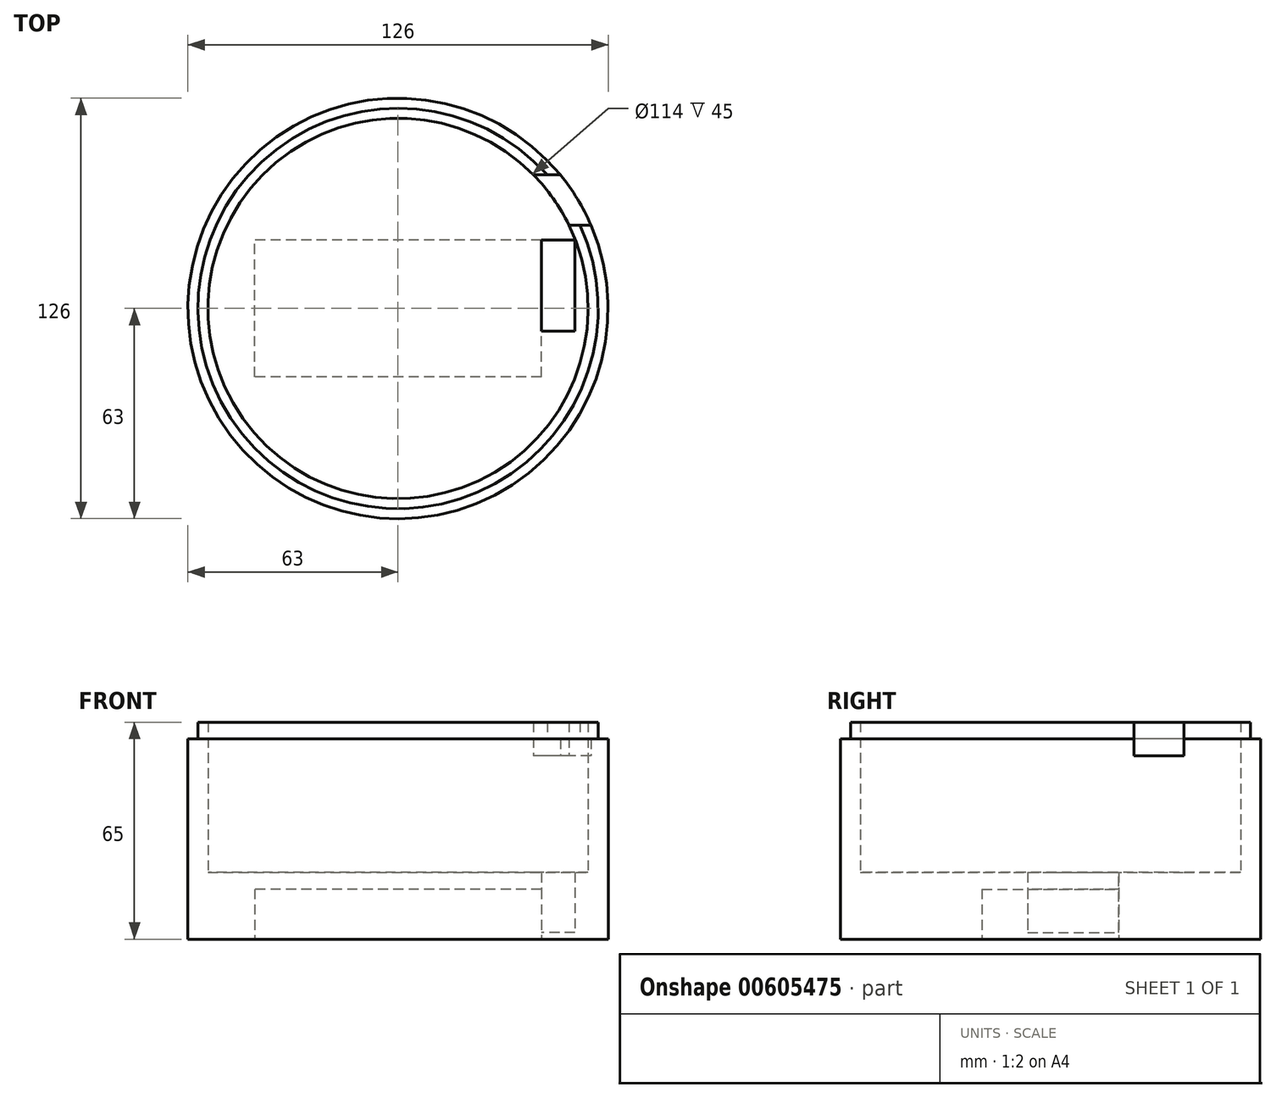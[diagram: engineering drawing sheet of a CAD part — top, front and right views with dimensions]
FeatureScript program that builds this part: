
annotation { "Feature Type Name" : "Feature", "Feature Type Description" : "" }
export const myFeature = defineFeature(function(context is Context, id is Id, definition is map)
    precondition{}
    {
        {
            var Q0;
            Q0=qCreatedBy(makeId("Top.planeOp"),FACE);
            var sketch = newSketch(context, id + "F0", { "sketchPlane" : qUnion([Q0])});
            skCircle(sketch, "E0", {"center": v(0, 0) * mm, "radius": 63 * mm});
            skCircle(sketch, "E1", {"center": v(0, 0) * mm, "radius": 60 * mm});
            skSolve(sketch);
        }
        {
            var Q0;
            Q0=qCreatedBy(makeId("Top.planeOp"),FACE);
            var sketch = newSketch(context, id + "F1", { "sketchPlane" : qUnion([Q0])});
            skCircle(sketch, "E2", {"center": v(0, 0) * mm, "radius": 57 * mm});
            skCircle(sketch, "E3", {"center": v(0, 0) * mm, "radius": 60 * mm});
            skSolve(sketch);
        }
        {
            var Q0;
            Q0=makeQuery(id+"F0.imprint","IMPRINT",FACE,{"disambiguationData":[TD([[makeQuery(id+"F0.imprint","IMPRINT",EDGE,{"derivedFrom":sQuery(id+"F0.wireOp",EDGE,"E0")}),1.0]])]});
            extrude(context, id + "F2", {"entities" : qUnion([Q0]), "depth" : 60 * mm, "offsetDistance" : 25 * mm});
        }
        {
            var Q0;
            Q0=qSketchRegion(id+"F1",true);
            extrude(context, id + "F3", {"entities" : qUnion([Q0]), "operationType" : NewBodyOperationType.ADD, "depth" : 65 * mm, "offsetDistance" : 25 * mm});
        }
        {
            var Q0;
            Q0=qCreatedBy(makeId("Top.planeOp"),FACE);
            var sketch = newSketch(context, id + "F4", { "sketchPlane" : qUnion([Q0])});
            skCircle(sketch, "E4", {"center": v(0, 0) * mm, "radius": 57 * mm});
            skSolve(sketch);
        }
        {
            var Q0;
            Q0=qSketchRegion(id+"F4",true);
            var Q1;
            Q1=qSketchRegion(id+"F7",true);
            extrude(context, id + "F5", {"entities" : qUnion([Q0, Q1]), "operationType" : NewBodyOperationType.ADD, "depth" : 60 * mm, "offsetDistance" : 25 * mm});
        }
        {
            var Q0;
            Q0=qCreatedBy(makeId("Top.planeOp"),FACE);
            cPlane(context, id + "F6", {"entities" : qUnion([Q0]), "cplaneType" : CPlaneType.OFFSET, "offset" : 45 * mm, "width" : 150 * mm, "height" : 150 * mm});
        }
        {
            var Q0;
            Q0=qCreatedBy(id+"F6.planeOp",FACE);
            var sketch = newSketch(context, id + "F7", { "sketchPlane" : qUnion([Q0])});
            skCircle(sketch, "E5", {"center": v(0, 0) * mm, "radius": 57 * mm});
            skSolve(sketch);
        }
        {
            var Q0;
            Q0=qSketchRegion(id+"F7",true);
            extrude(context, id + "F8", {"entities" : qUnion([Q0]), "operationType" : NewBodyOperationType.REMOVE, "oppositeDirection" : true, "depth" : 40 * mm, "offsetDistance" : 25 * mm});
        }
        {
            var Q0;
            Q0=qCreatedBy(makeId("Right.planeOp"),FACE);
            var sketch = newSketch(context, id + "F9", { "sketchPlane" : qUnion([Q0])});
            skLineSegment(sketch, "E6", {"start": v(0, 0) * mm, "end": v(25, 0) * mm, "construction": true});
            skLineSegment(sketch, "E7", {"start": v(25, 0) * mm, "end": v(25, 65) * mm, "construction": true});
            skLineSegment(sketch, "E8.bottom", {"start": v(25, 65) * mm, "end": v(40, 65) * mm});
            skLineSegment(sketch, "E8.top", {"start": v(25, 55) * mm, "end": v(40, 55) * mm});
            skLineSegment(sketch, "E8.left", {"start": v(25, 65) * mm, "end": v(25, 55) * mm});
            skLineSegment(sketch, "E8.right", {"start": v(40, 65) * mm, "end": v(40, 55) * mm});
            skSolve(sketch);
        }
        {
            var Q0;
            Q0=makeQuery(id+"F9.imprint","IMPRINT",FACE,{"disambiguationData":[TD([[makeQuery(id+"F9.imprint","IMPRINT",EDGE,{"derivedFrom":sQuery(id+"F9.wireOp",EDGE,"E8.bottom")}),-1.0]])]});
            extrude(context, id + "F10", {"entities" : qUnion([Q0]), "operationType" : NewBodyOperationType.REMOVE, "depth" : 279.5 * mm, "offsetDistance" : 25 * mm});
        }
        {
            var Q0;
            Q0=makeQuery(id+"F1.imprint","IMPRINT",FACE,{"disambiguationData":[TD([[makeQuery(id+"F1.imprint","IMPRINT",EDGE,{"derivedFrom":sQuery(id+"F1.wireOp",EDGE,"E2")}),1.0]])]});
            extrude(context, id + "F11", {"entities" : qUnion([Q0]), "operationType" : NewBodyOperationType.REMOVE, "depth" : 71.5 * mm, "offsetDistance" : 25 * mm});
        }
        {
            var Q0;
            Q0=qCreatedBy(makeId("Top.planeOp"),FACE);
            cPlane(context, id + "F12", {"entities" : qUnion([Q0]), "cplaneType" : CPlaneType.OFFSET, "offset" : 15 * mm, "width" : 150 * mm, "height" : 150 * mm});
        }
        {
            var Q0;
            Q0=qCreatedBy(makeId("Top.planeOp"),FACE);
            var sketch = newSketch(context, id + "F13", { "sketchPlane" : qUnion([Q0])});
            skCircle(sketch, "E9", {"center": v(0, 0) * mm, "radius": 63 * mm});
            skSolve(sketch);
        }
        {
            var Q0;
            Q0=qSketchRegion(id+"F13",true);
            extrude(context, id + "F14", {"entities" : qUnion([Q0]), "operationType" : NewBodyOperationType.ADD, "depth" : 20 * mm, "offsetDistance" : 25 * mm});
        }
        {
            var Q0;
            Q0=qCreatedBy(makeId("Top.planeOp"),FACE);
            var sketch = newSketch(context, id + "F15", { "sketchPlane" : qUnion([Q0])});
            skLineSegment(sketch, "E10.bottom", {"start": v(43, -20.5) * mm, "end": v(-43, -20.5) * mm});
            skLineSegment(sketch, "E10.top", {"start": v(43, 20.5) * mm, "end": v(-43, 20.5) * mm});
            skLineSegment(sketch, "E10.left", {"start": v(43, -20.5) * mm, "end": v(43, 20.5) * mm});
            skLineSegment(sketch, "E10.right", {"start": v(-43, -20.5) * mm, "end": v(-43, 20.5) * mm});
            skPoint(sketch, "E10.middle", {"position": v(0, 0) * mm});
            skSolve(sketch);
        }
        {
            var Q0;
            Q0=makeQuery(id+"F15.imprint","IMPRINT",FACE,{"disambiguationData":[TD([[makeQuery(id+"F15.imprint","IMPRINT",EDGE,{"derivedFrom":sQuery(id+"F15.wireOp",EDGE,"E10.bottom")}),-1.0]])]});
            var Q1;
            Q1=qSketchRegion(id+"F17",true);
            extrude(context, id + "F16", {"entities" : qUnion([Q0, Q1]), "operationType" : NewBodyOperationType.REMOVE, "depth" : 15 * mm, "offsetDistance" : 25 * mm});
        }
        {
            var Q0;
            Q0=qCreatedBy(makeId("Right.planeOp"),FACE);
            var sketch = newSketch(context, id + "F17", { "sketchPlane" : qUnion([Q0])});
            skLineSegment(sketch, "E11", {"start": v(0, 0) * mm, "end": v(-6.83, 0) * mm, "construction": true});
            skLineSegment(sketch, "E12", {"start": v(-6.83, 0) * mm, "end": v(-6.83, 2) * mm, "construction": true});
            skLineSegment(sketch, "E13", {"start": v(-6.83, 2) * mm, "end": v(20.47, 2) * mm});
            skLineSegment(sketch, "E14", {"start": v(20.47, 2) * mm, "end": v(20.47, 15) * mm});
            skLineSegment(sketch, "E15", {"start": v(20.47, 15) * mm, "end": v(-6.83, 15) * mm});
            skLineSegment(sketch, "E16", {"start": v(-6.83, 15) * mm, "end": v(-6.83, 2) * mm});
            skSolve(sketch);
        }
        {
            var Q0;
            Q0=qSketchRegion(id+"F17",true);
            extrude(context, id + "F18", {"entities" : qUnion([Q0]), "operationType" : NewBodyOperationType.REMOVE, "depth" : 53 * mm, "offsetDistance" : 25 * mm});
        }
        {
            var Q0;
            Q0=qCreatedBy(id+"F12.planeOp",FACE);
            var sketch = newSketch(context, id + "F19", { "sketchPlane" : qUnion([Q0])});
            skLineSegment(sketch, "E17", {"start": v(0, 0) * mm, "end": v(43, 0) * mm, "construction": true});
            skLineSegment(sketch, "E18", {"start": v(43, 0) * mm, "end": v(43, -6.83) * mm});
            skLineSegment(sketch, "E19", {"start": v(43, -6.83) * mm, "end": v(53, -6.83) * mm});
            skLineSegment(sketch, "E20", {"start": v(53, -6.83) * mm, "end": v(53, 20.47) * mm});
            skLineSegment(sketch, "E21", {"start": v(53, 20.47) * mm, "end": v(43, 20.47) * mm});
            skLineSegment(sketch, "E22", {"start": v(43, 20.47) * mm, "end": v(43, 0) * mm});
            skSolve(sketch);
        }
        {
            var Q0;
            Q0=qSketchRegion(id+"F19",true);
            extrude(context, id + "F20", {"entities" : qUnion([Q0]), "operationType" : NewBodyOperationType.REMOVE, "depth" : 25 * mm, "offsetDistance" : 25 * mm});
        }
    });
